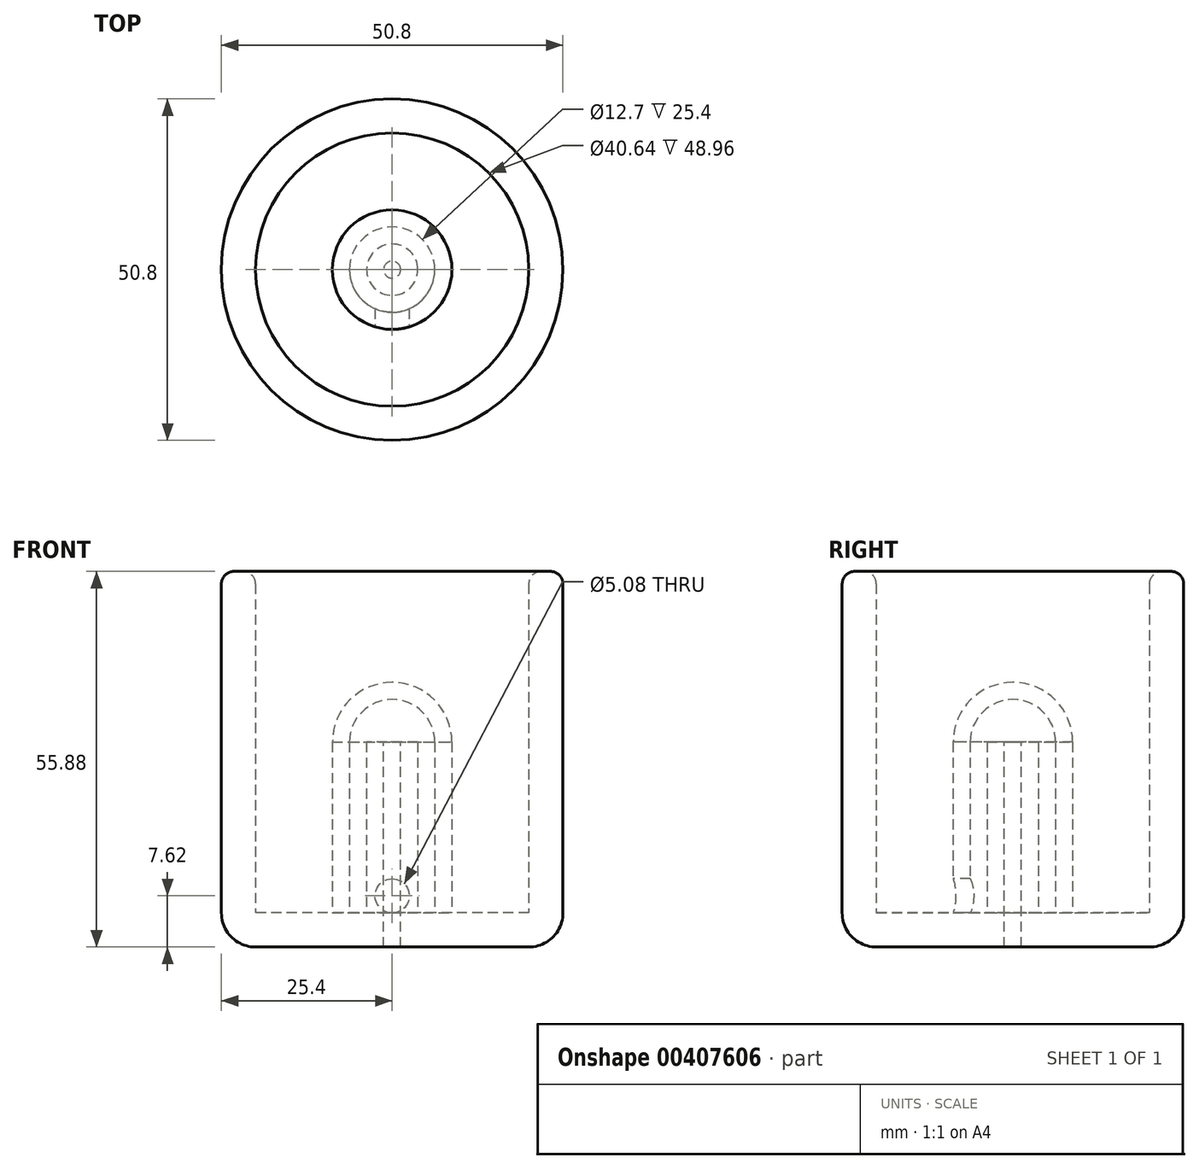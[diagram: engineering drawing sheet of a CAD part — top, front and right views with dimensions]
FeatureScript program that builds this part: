
annotation { "Feature Type Name" : "Feature", "Feature Type Description" : "" }
export const myFeature = defineFeature(function(context is Context, id is Id, definition is map)
    precondition{}
    {
        {
            var Q0;
            Q0=qCreatedBy(makeId("Top.planeOp"),FACE);
            var sketch = newSketch(context, id + "F0", { "sketchPlane" : qUnion([Q0])});
            skCircle(sketch, "E0", {"center": v(0, 0) * mm, "radius": 25.4 * mm});
            skCircle(sketch, "E1", {"center": v(0, 0) * mm, "radius": 20.32 * mm});
            skCircle(sketch, "E2", {"center": v(0, 0) * mm, "radius": 1.27 * mm});
            skCircle(sketch, "E3", {"center": v(0, 0) * mm, "radius": 3.81 * mm});
            skCircle(sketch, "E4", {"center": v(0, 0) * mm, "radius": 6.35 * mm});
            skCircle(sketch, "E5", {"center": v(0, 0) * mm, "radius": 8.9 * mm});
            skPoint(sketch, "E6", {"position": v(0, -8.9) * mm});
            skPoint(sketch, "E7", {"position": v(8.9, 0) * mm});
            skPoint(sketch, "E8", {"position": v(0, 8.9) * mm});
            skPoint(sketch, "E9", {"position": v(-8.9, 0) * mm});
            skSolve(sketch);
        }
        {
            var Q0;
            Q0=makeQuery(id+"F0.imprint","IMPRINT",FACE,{"disambiguationData":[TD([[makeQuery(id+"F0.imprint","IMPRINT",EDGE,{"derivedFrom":sQuery(id+"F0.wireOp",EDGE,"E0")}),1.0]])]});
            var Q1;
            Q1=makeQuery(id+"F0.imprint","IMPRINT",FACE,{"disambiguationData":[TD([[makeQuery(id+"F0.imprint","IMPRINT",EDGE,{"derivedFrom":sQuery(id+"F0.wireOp",EDGE,"E1")}),1.0]])]});
            var Q2;
            Q2=makeQuery(id+"F0.imprint","IMPRINT",FACE,{"disambiguationData":[TD([[makeQuery(id+"F0.imprint","IMPRINT",EDGE,{"derivedFrom":sQuery(id+"F0.wireOp",EDGE,"E3")}),-1.0]])]});
            var Q3;
            Q3=makeQuery(id+"F0.imprint","IMPRINT",FACE,{"disambiguationData":[TD([[makeQuery(id+"F0.imprint","IMPRINT",EDGE,{"derivedFrom":sQuery(id+"F0.wireOp",EDGE,"E4")}),-1.0]])]});
            var Q4;
            Q4=makeQuery(id+"F0.imprint","IMPRINT",FACE,{"disambiguationData":[TD([[makeQuery(id+"F0.imprint","IMPRINT",EDGE,{"derivedFrom":sQuery(id+"F0.wireOp",EDGE,"E2")}),-1.0]])]});
            extrude(context, id + "F1", {"entities" : qUnion([Q0, Q1, Q2, Q3, Q4]), "depth" : -5.08 * mm});
        }
        {
            var Q0;
            Q0=makeQuery(id+"F0.imprint","IMPRINT",FACE,{"disambiguationData":[TD([[makeQuery(id+"F0.imprint","IMPRINT",EDGE,{"derivedFrom":sQuery(id+"F0.wireOp",EDGE,"E4")}),-1.0]])]});
            extrude(context, id + "F2", {"entities" : qUnion([Q0]), "operationType" : NewBodyOperationType.ADD, "depth" : 25.4 * mm});
        }
        {
            var Q0;
            Q0=makeQuery(id+"F0.imprint","IMPRINT",FACE,{"disambiguationData":[TD([[makeQuery(id+"F0.imprint","IMPRINT",EDGE,{"derivedFrom":sQuery(id+"F0.wireOp",EDGE,"E0")}),1.0]])]});
            extrude(context, id + "F3", {"entities" : qUnion([Q0]), "operationType" : NewBodyOperationType.ADD, "depth" : 50.8 * mm});
        }
        {
            var Q0;
            Q0=makeQuery(id+"F0.imprint","IMPRINT",FACE,{"disambiguationData":[TD([[makeQuery(id+"F0.imprint","IMPRINT",EDGE,{"derivedFrom":sQuery(id+"F0.wireOp",EDGE,"E2")}),-1.0]])]});
            extrude(context, id + "F4", {"entities" : qUnion([Q0]), "operationType" : NewBodyOperationType.ADD, "depth" : 25.4 * mm});
        }
        {
            var Q0;
            Q0=makeQuery(id+"F2.opExtrude","CAP_FACE",FACE,{"disambiguationData":[OSD([sQuery(id+"F0.wireOp",EDGE,"E4"),sQuery(id+"F0.wireOp",EDGE,"E5")])],"isStart":false});
            var sketch = newSketch(context, id + "F5", { "sketchPlane" : qUnion([Q0])});
            skArc(sketch, "E10", {"start": v(-6.35, 0) * mm, "mid": v(0, 6.35) * mm, "end": v(6.35, 0) * mm});
            skLineSegment(sketch, "E11", {"start": v(-6.35, 0) * mm, "end": v(6.35, 0) * mm});
            skLineSegment(sketch, "E12", {"start": v(6.35, 0) * mm, "end": v(8.9, 0) * mm});
            skLineSegment(sketch, "E13", {"start": v(-6.35, 0) * mm, "end": v(-8.9, 0) * mm});
            skSolve(sketch);
        }
        {
            var Q0;
            Q0=makeQuery(id+"F5.imprint","IMPRINT",FACE,{"disambiguationData":[TD([[makeQuery(id+"F5.imprint","IMPRINT",EDGE,{"derivedFrom":sQuery(id+"F5.wireOp",EDGE,"E10")}),-1.0]])]});
            var Q1;
            Q1=sQuery(id+"F5.wireOp",EDGE,"E10");
            var Q2;
            Q2=sQuery(id+"F5.wireOp",EDGE,"E11");
            revolve(context, id + "F6", {"entities" : qUnion([Q0]), "surfaceEntities" : qUnion([Q1]), "axis" : qUnion([Q2]), "revolveType" : RevolveType.ONE_DIRECTION, "angle" : 180 * degree});
        }
        {
            var Q0;
            Q0=qCreatedBy(makeId("Front.planeOp"),FACE);
            cPlane(context, id + "F7", {"entities" : qUnion([Q0]), "cplaneType" : CPlaneType.OFFSET, "offset" : 8.9 * mm, "width" : 152.4 * mm, "height" : 152.4 * mm});
        }
        {
            var Q0;
            Q0=qCreatedBy(id+"F7.planeOp",FACE);
            var sketch = newSketch(context, id + "F8", { "sketchPlane" : qUnion([Q0])});
            skPoint(sketch, "E14", {"position": v(0, 2.54) * mm});
            skCircle(sketch, "E15", {"center": v(0, 2.54) * mm, "radius": 2.54 * mm});
            skSolve(sketch);
        }
        {
            var Q0;
            Q0=makeQuery(id+"F8.imprint","IMPRINT",FACE,{"disambiguationData":[TD([[makeQuery(id+"F8.imprint","IMPRINT",EDGE,{"derivedFrom":sQuery(id+"F8.wireOp",EDGE,"E15")}),1.0]])]});
            extrude(context, id + "F9", {"entities" : qUnion([Q0]), "operationType" : NewBodyOperationType.REMOVE, "oppositeDirection" : true, "depth" : 5.08 * mm});
        }
        {
            var Q0;
            Q0=makeQuery(id+"F3.opExtrude","CAP_EDGE",EDGE,{"disambiguationData":[OSD([sQuery(id+"F0.wireOp",EDGE,"E1")])],"isStart":false});
            var Q1;
            Q1=makeQuery(id+"F3.opExtrude","CAP_EDGE",EDGE,{"disambiguationData":[OSD([sQuery(id+"F0.wireOp",EDGE,"E0")])],"isStart":false});
            fillet(context, id + "F10", {"entities" : qUnion([Q0, Q1]), "radius" : 1.84 * mm, "tangentPropagation" : true, "allowEdgeOverflow" : false});
        }
        {
            var Q0;
            Q0=makeQuery(id+"F1.opExtrude","CAP_EDGE",EDGE,{"disambiguationData":[OSD([sQuery(id+"F0.wireOp",EDGE,"E0")])],"isStart":false});
            var Q1;
            Q1=makeQuery(id+"F3.opExtrude","CAP_EDGE",EDGE,{"disambiguationData":[OSD([sQuery(id+"F0.wireOp",EDGE,"E1")])],"isStart":true});
            fillet(context, id + "F11", {"entities" : qUnion([Q0, Q1]), "radius" : 5.08 * mm, "tangentPropagation" : true, "allowEdgeOverflow" : false});
        }
    });
